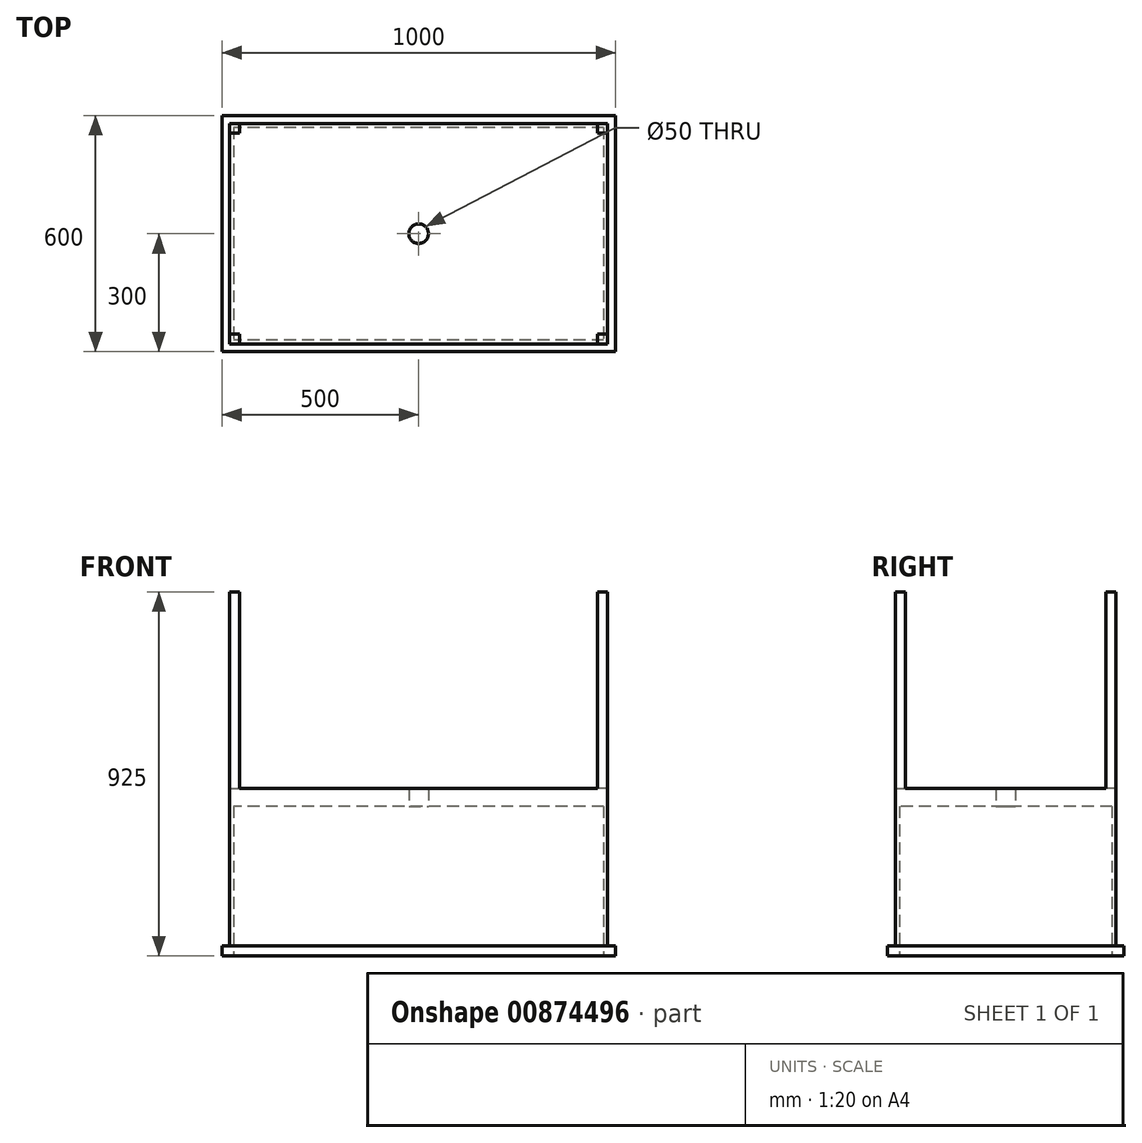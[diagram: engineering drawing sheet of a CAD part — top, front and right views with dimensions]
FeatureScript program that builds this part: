
annotation { "Feature Type Name" : "Feature", "Feature Type Description" : "" }
export const myFeature = defineFeature(function(context is Context, id is Id, definition is map)
    precondition{}
    {
        {
            var Q0;
            Q0=qCreatedBy(makeId("Top.planeOp"),FACE);
            var sketch = newSketch(context, id + "F0", { "sketchPlane" : qUnion([Q0])});
            skLineSegment(sketch, "E0.bottom", {"start": v(500, -300) * mm, "end": v(-500, -300) * mm});
            skLineSegment(sketch, "E0.top", {"start": v(500, 300) * mm, "end": v(-500, 300) * mm});
            skLineSegment(sketch, "E0.left", {"start": v(500, -300) * mm, "end": v(500, 300) * mm});
            skLineSegment(sketch, "E0.right", {"start": v(-500, -300) * mm, "end": v(-500, 300) * mm});
            skPoint(sketch, "E0.middle", {"position": v(0, 0) * mm});
            skSolve(sketch);
        }
        {
            var Q0;
            Q0 = qSketchRegion(id + "F0", true);
            extrude(context, id + "F1", {"entities" : qUnion([Q0]), "depth" : 25 * mm, "offsetDistance" : 25 * mm});
        }
        {
            var Q0;
            Q0=makeQuery(id+"F1.opExtrude","CAP_FACE",FACE,{"disambiguationData":[OSD([sQuery(id+"F0.wireOp",EDGE,"E0.bottom"),sQuery(id+"F0.wireOp",EDGE,"E0.top"),sQuery(id+"F0.wireOp",EDGE,"E0.left"),sQuery(id+"F0.wireOp",EDGE,"E0.right")])],"isStart":false});
            var sketch = newSketch(context, id + "F2", { "sketchPlane" : qUnion([Q0])});
            skLineSegment(sketch, "E1.bottom", {"start": v(480, -280) * mm, "end": v(-480, -280) * mm});
            skLineSegment(sketch, "E1.top", {"start": v(480, 280) * mm, "end": v(-480, 280) * mm});
            skLineSegment(sketch, "E1.left", {"start": v(480, -280) * mm, "end": v(480, 280) * mm});
            skLineSegment(sketch, "E1.right", {"start": v(-480, -280) * mm, "end": v(-480, 280) * mm});
            skPoint(sketch, "E1.middle", {"position": v(0, 0) * mm});
            skSolve(sketch);
        }
        {
            var Q0;
            Q0 = qSketchRegion(id + "F2", true);
            extrude(context, id + "F3", {"entities" : qUnion([Q0]), "operationType" : NewBodyOperationType.ADD, "depth" : 400 * mm, "offsetDistance" : 25 * mm});
        }
        {
            var Q0;
            Q0=makeQuery(id+"F1.opExtrude","CAP_FACE",FACE,{"disambiguationData":[OSD([sQuery(id+"F0.wireOp",EDGE,"E0.bottom"),sQuery(id+"F0.wireOp",EDGE,"E0.top"),sQuery(id+"F0.wireOp",EDGE,"E0.left"),sQuery(id+"F0.wireOp",EDGE,"E0.right")])],"isStart":true});
            var sketch = newSketch(context, id + "F4", { "sketchPlane" : qUnion([Q0])});
            skLineSegment(sketch, "E2.bottom", {"start": v(470, -270) * mm, "end": v(-470, -270) * mm});
            skLineSegment(sketch, "E2.top", {"start": v(470, 270) * mm, "end": v(-470, 270) * mm});
            skLineSegment(sketch, "E2.left", {"start": v(470, -270) * mm, "end": v(470, 270) * mm});
            skLineSegment(sketch, "E2.right", {"start": v(-470, -270) * mm, "end": v(-470, 270) * mm});
            skPoint(sketch, "E2.middle", {"position": v(0, 0) * mm});
            skSolve(sketch);
        }
        {
            var Q0;
            Q0 = qSketchRegion(id + "F4", true);
            extrude(context, id + "F5", {"entities" : qUnion([Q0]), "operationType" : NewBodyOperationType.REMOVE, "oppositeDirection" : true, "depth" : 380 * mm, "offsetDistance" : 25 * mm});
        }
        {
            var Q0;
            Q0=makeQuery(id+"F3.opExtrude","CAP_FACE",FACE,{"disambiguationData":[OSD([sQuery(id+"F2.wireOp",EDGE,"E1.bottom"),sQuery(id+"F2.wireOp",EDGE,"E1.top"),sQuery(id+"F2.wireOp",EDGE,"E1.left"),sQuery(id+"F2.wireOp",EDGE,"E1.right")])],"isStart":false});
            var sketch = newSketch(context, id + "F6", { "sketchPlane" : qUnion([Q0])});
            skLineSegment(sketch, "E3.bottom", {"start": v(-480, 280) * mm, "end": v(-455, 280) * mm});
            skLineSegment(sketch, "E3.top", {"start": v(-480, 255) * mm, "end": v(-455, 255) * mm});
            skLineSegment(sketch, "E3.left", {"start": v(-480, 280) * mm, "end": v(-480, 255) * mm});
            skLineSegment(sketch, "E3.right", {"start": v(-455, 280) * mm, "end": v(-455, 255) * mm});
            skLineSegment(sketch, "E4.bottom", {"start": v(-480, -280) * mm, "end": v(-455, -280) * mm});
            skLineSegment(sketch, "E4.top", {"start": v(-480, -255) * mm, "end": v(-455, -255) * mm});
            skLineSegment(sketch, "E4.left", {"start": v(-480, -280) * mm, "end": v(-480, -255) * mm});
            skLineSegment(sketch, "E4.right", {"start": v(-455, -280) * mm, "end": v(-455, -255) * mm});
            skLineSegment(sketch, "E5.bottom", {"start": v(480, -280) * mm, "end": v(455, -280) * mm});
            skLineSegment(sketch, "E5.top", {"start": v(480, -255) * mm, "end": v(455, -255) * mm});
            skLineSegment(sketch, "E5.left", {"start": v(480, -280) * mm, "end": v(480, -255) * mm});
            skLineSegment(sketch, "E5.right", {"start": v(455, -280) * mm, "end": v(455, -255) * mm});
            skLineSegment(sketch, "E6.bottom", {"start": v(480, 280) * mm, "end": v(455, 280) * mm});
            skLineSegment(sketch, "E6.top", {"start": v(480, 255) * mm, "end": v(455, 255) * mm});
            skLineSegment(sketch, "E6.left", {"start": v(480, 280) * mm, "end": v(480, 255) * mm});
            skLineSegment(sketch, "E6.right", {"start": v(455, 280) * mm, "end": v(455, 255) * mm});
            skSolve(sketch);
        }
        {
            var Q0;
            Q0 = qSketchRegion(id + "F6", true);
            extrude(context, id + "F7", {"entities" : qUnion([Q0]), "operationType" : NewBodyOperationType.ADD, "depth" : 500 * mm, "offsetDistance" : 25 * mm});
        }
        {
            var Q0;
            Q0=makeQuery(id+"F5.boolean.opBoolean","COPY",FACE,{"derivedFrom":makeQuery(id+"F5.opExtrude","CAP_FACE",FACE,{"disambiguationData":[OSD([sQuery(id+"F4.wireOp",EDGE,"E2.bottom"),sQuery(id+"F4.wireOp",EDGE,"E2.top"),sQuery(id+"F4.wireOp",EDGE,"E2.left"),sQuery(id+"F4.wireOp",EDGE,"E2.right")])],"isStart":false})});
            var sketch = newSketch(context, id + "F8", { "sketchPlane" : qUnion([Q0])});
            skCircle(sketch, "E7", {"center": v(0, 0) * mm, "radius": 25 * mm});
            skSolve(sketch);
        }
        {
            var Q0;
            Q0 = qSketchRegion(id + "F8", true);
            extrude(context, id + "F9", {"entities" : qUnion([Q0]), "operationType" : NewBodyOperationType.REMOVE, "oppositeDirection" : true, "depth" : 100 * mm, "offsetDistance" : 25 * mm});
        }
    });
